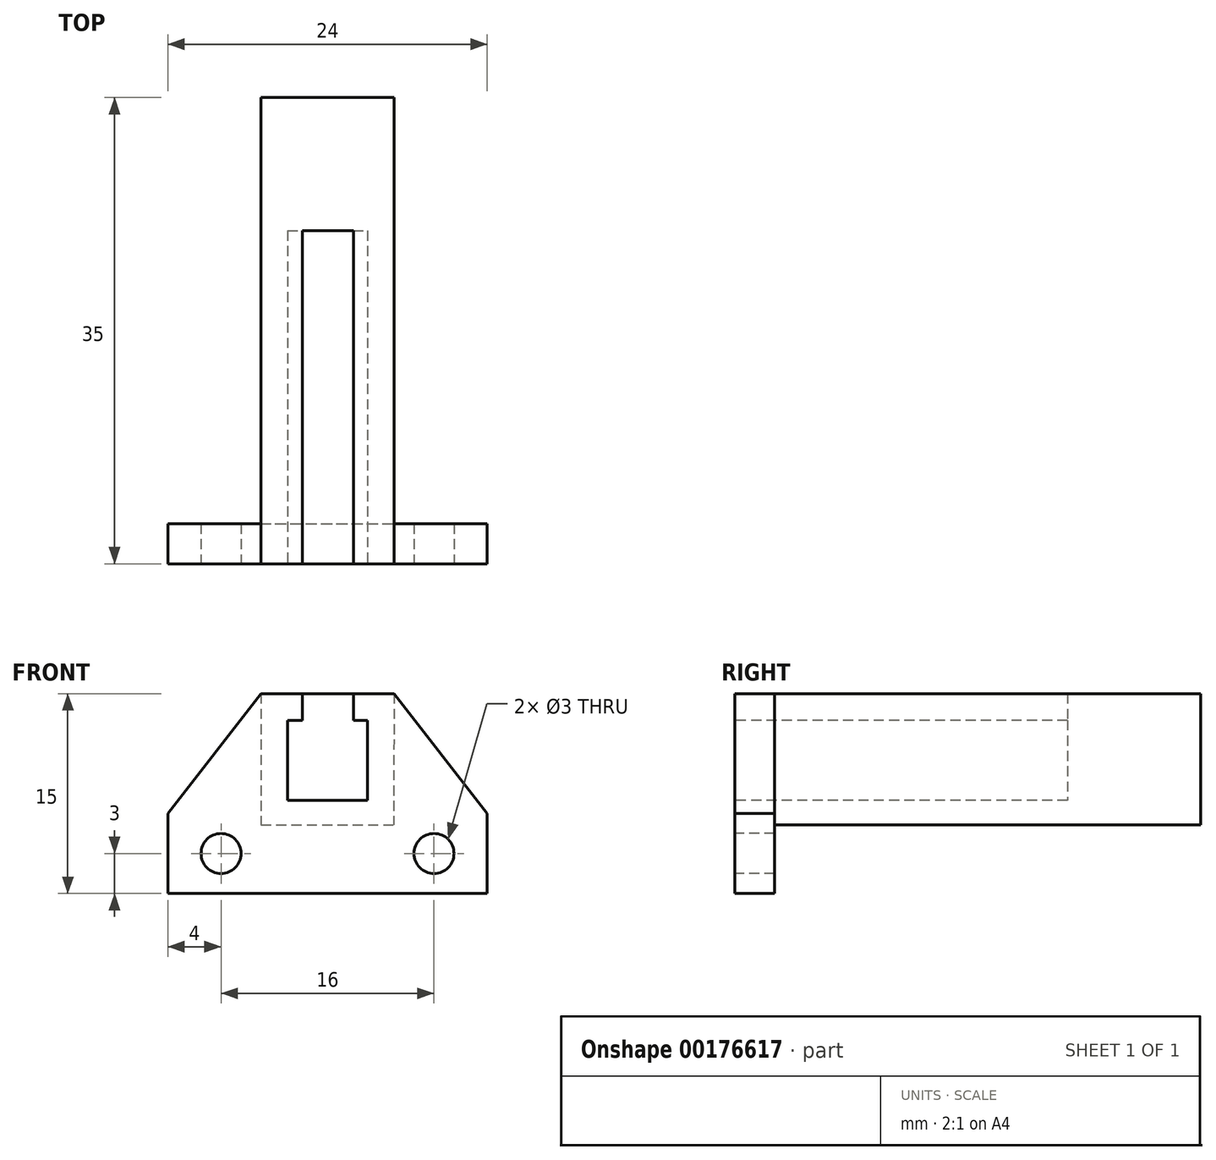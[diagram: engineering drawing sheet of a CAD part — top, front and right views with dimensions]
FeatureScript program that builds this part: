
annotation { "Feature Type Name" : "Feature", "Feature Type Description" : "" }
export const myFeature = defineFeature(function(context is Context, id is Id, definition is map)
    precondition{}
    {
        {
            var Q0;
            Q0=qCreatedBy(makeId("Front.planeOp"),FACE);
            var sketch = newSketch(context, id + "F0", { "sketchPlane" : qUnion([Q0])});
            skLineSegment(sketch, "E0", {"start": v(7, 0) * mm, "end": v(0, -9) * mm});
            skLineSegment(sketch, "E1", {"start": v(0, -9) * mm, "end": v(0, -15) * mm});
            skLineSegment(sketch, "E2", {"start": v(0, -15) * mm, "end": v(24, -15) * mm});
            skLineSegment(sketch, "E3", {"start": v(24, -15) * mm, "end": v(24, -9) * mm});
            skLineSegment(sketch, "E4", {"start": v(24, -9) * mm, "end": v(17, 0) * mm});
            skLineSegment(sketch, "E5", {"start": v(17, 0) * mm, "end": v(7, 0) * mm});
            skCircle(sketch, "E6", {"center": v(4, -12) * mm, "radius": 1.5 * mm});
            skCircle(sketch, "E7", {"center": v(20, -12) * mm, "radius": 1.5 * mm});
            skLineSegment(sketch, "E8.bottom", {"start": v(9, -2) * mm, "end": v(15, -2) * mm});
            skLineSegment(sketch, "E8.top", {"start": v(9, -8) * mm, "end": v(15, -8) * mm});
            skLineSegment(sketch, "E8.left", {"start": v(9, -2) * mm, "end": v(9, -8) * mm});
            skLineSegment(sketch, "E8.right", {"start": v(15, -2) * mm, "end": v(15, -8) * mm});
            skLineSegment(sketch, "E9", {"start": v(7, 0) * mm, "end": v(7, -9.87) * mm});
            skLineSegment(sketch, "E10", {"start": v(7, -9.87) * mm, "end": v(16.96, -9.87) * mm});
            skLineSegment(sketch, "E11", {"start": v(17, 0) * mm, "end": v(16.96, -9.87) * mm});
            skLineSegment(sketch, "E12", {"start": v(10.13, 0) * mm, "end": v(10.13, -2) * mm});
            skLineSegment(sketch, "E13", {"start": v(13.94, 0) * mm, "end": v(13.94, -2) * mm});
            skSolve(sketch);
        }
        {
            var Q0;
            Q0 = qSketchRegion(id + "F0", true);
            var Q1;
            Q1=makeQuery(id+"F0.imprint","IMPRINT",FACE,{"disambiguationData":[TD([[makeQuery(id+"F0.imprint","IMPRINT",EDGE,{"derivedFrom":sQuery(id+"F0.wireOp",EDGE,"E0")}),1.0]])]});
            var Q2;
            Q2=makeQuery(id+"F0.imprint","IMPRINT",FACE,{"disambiguationData":[TD([[makeQuery(id+"F0.imprint","IMPRINT",EDGE,{"derivedFrom":sQuery(id+"F0.wireOp",EDGE,"E8.top")}),1.0]])]});
            extrude(context, id + "F1", {"entities" : qUnion([Q0, Q1, Q2]), "oppositeDirection" : true, "depth" : 3 * mm});
        }
        {
            var Q0;
            Q0=makeQuery(id+"F0.imprint","IMPRINT",FACE,{"disambiguationData":[TD([[makeQuery(id+"F0.imprint","IMPRINT",EDGE,{"derivedFrom":sQuery(id+"F0.wireOp",EDGE,"E8.top")}),-1.0]])]});
            var Q1;
            Q1=makeQuery(id+"F0.imprint","IMPRINT",FACE,{"disambiguationData":[TD([[makeQuery(id+"F0.imprint","IMPRINT",EDGE,{"derivedFrom":sQuery(id+"F0.wireOp",EDGE,"E8.top")}),1.0]])]});
            var Q2;
            {var subQ0=sQuery(id+"F0.wireOp",EDGE,"E12");Q2=makeQuery(id+"F0.imprint","IMPRINT",FACE,{"disambiguationData":[TD([[makeQuery(id+"F0.imprint","IMPRINT",EDGE,{"derivedFrom":subQ0}),1.0]])]});}
            extrude(context, id + "F2", {"entities" : qUnion([Q0, Q1, Q2]), "operationType" : NewBodyOperationType.ADD, "oppositeDirection" : true, "depth" : 35 * mm});
        }
        {
            var Q0;
            {var subQ0=sQuery(id+"F0.wireOp",EDGE,"E12");Q0=makeQuery(id+"F0.imprint","IMPRINT",FACE,{"disambiguationData":[TD([[makeQuery(id+"F0.imprint","IMPRINT",EDGE,{"derivedFrom":subQ0}),1.0]])]});}
            var Q1;
            Q1=makeQuery(id+"F0.imprint","IMPRINT",FACE,{"disambiguationData":[TD([[makeQuery(id+"F0.imprint","IMPRINT",EDGE,{"derivedFrom":sQuery(id+"F0.wireOp",EDGE,"E8.top")}),1.0]])]});
            extrude(context, id + "F3", {"entities" : qUnion([Q0, Q1]), "operationType" : NewBodyOperationType.REMOVE, "oppositeDirection" : true, "depth" : 25 * mm});
        }
    });
